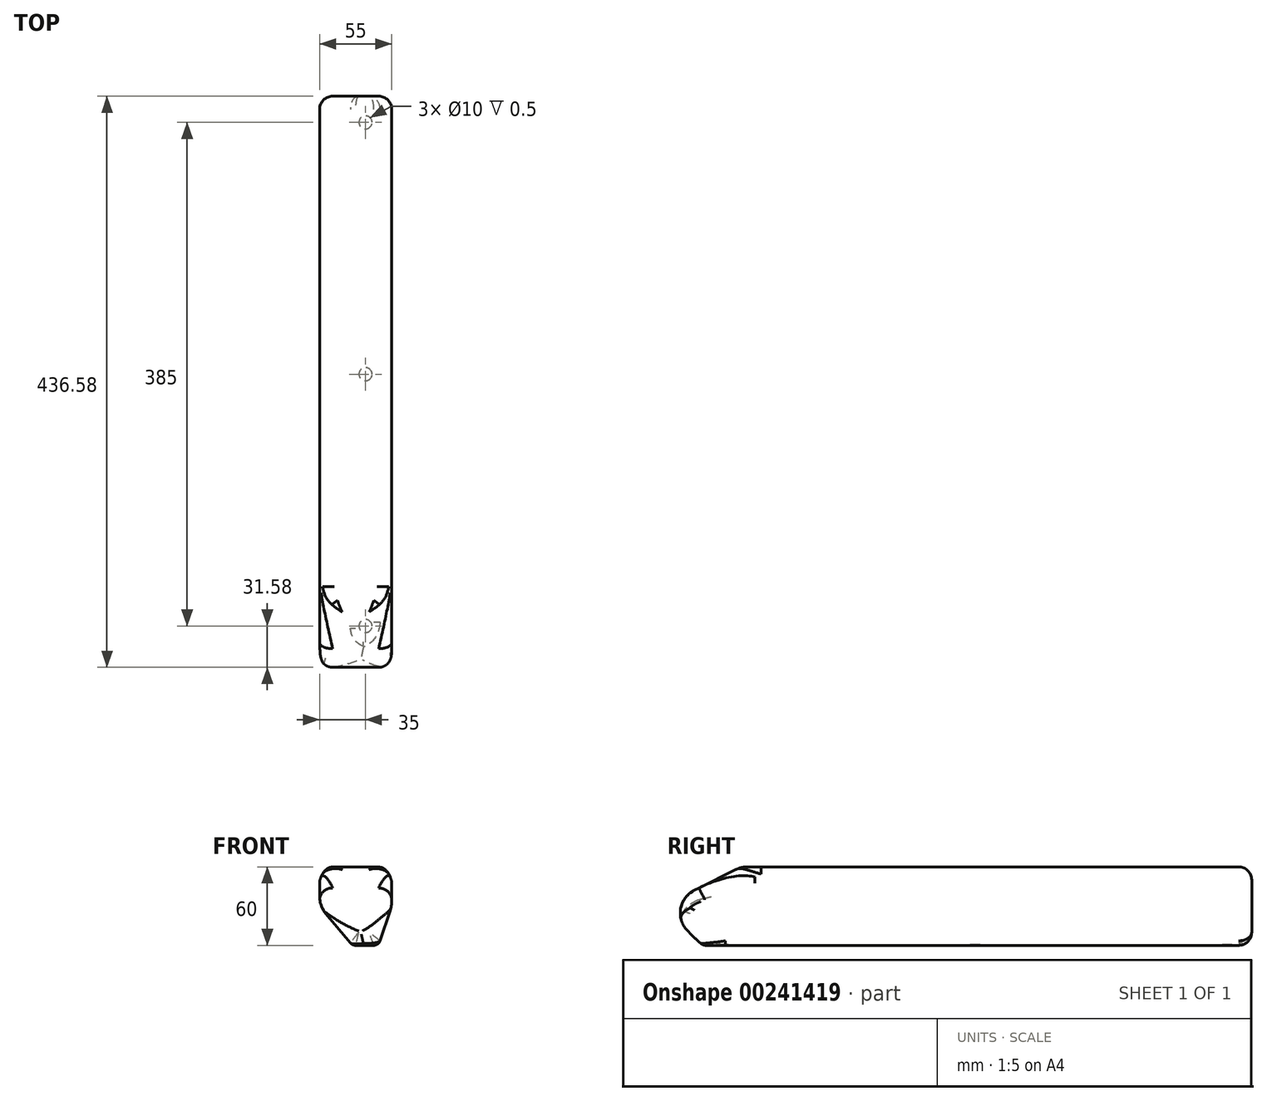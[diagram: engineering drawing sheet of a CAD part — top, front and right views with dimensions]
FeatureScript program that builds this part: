
annotation { "Feature Type Name" : "Feature", "Feature Type Description" : "" }
export const myFeature = defineFeature(function(context is Context, id is Id, definition is map)
    precondition{}
    {
        {
            var Q0;
            Q0=qCreatedBy(makeId("Top.planeOp"),FACE);
            var sketch = newSketch(context, id + "F0", { "sketchPlane" : qUnion([Q0])});
            skLineSegment(sketch, "E0.bottom", {"start": v(-27.5, 212.5) * mm, "end": v(27.5, 212.5) * mm});
            skLineSegment(sketch, "E0.top", {"start": v(-27.5, -237.5) * mm, "end": v(27.5, -237.5) * mm});
            skLineSegment(sketch, "E0.left", {"start": v(-27.5, 212.5) * mm, "end": v(-27.5, -237.5) * mm});
            skLineSegment(sketch, "E0.right", {"start": v(27.5, 212.5) * mm, "end": v(27.5, -237.5) * mm});
            skPoint(sketch, "E0.middle", {"position": v(0, 8.95) * mm});
            skSolve(sketch);
        }
        {
            var Q0;
            Q0=qSketchRegion(id+"F0",true);
            extrude(context, id + "F1", {"entities" : qUnion([Q0]), "depth" : 60 * mm});
        }
        {
            var Q0;
            Q0=makeQuery(id+"F1.opExtrude","CAP_FACE",FACE,{"disambiguationData":[OSD([sQuery(id+"F0.wireOp",EDGE,"E0.bottom"),sQuery(id+"F0.wireOp",EDGE,"E0.top"),sQuery(id+"F0.wireOp",EDGE,"E0.left"),sQuery(id+"F0.wireOp",EDGE,"E0.right")])],"isStart":true});
            var sketch = newSketch(context, id + "F2", { "sketchPlane" : qUnion([Q0])});
            skCircle(sketch, "E1", {"center": v(7.5, 192.5) * mm, "radius": 5 * mm});
            skCircle(sketch, "E2", {"center": v(7.5, -192.5) * mm, "radius": 5 * mm});
            skCircle(sketch, "E3", {"center": v(7.5, 0) * mm, "radius": 5 * mm});
            skSolve(sketch);
        }
        {
            var Q0;
            Q0=qSketchRegion(id+"F2",true);
            extrude(context, id + "F3", {"entities" : qUnion([Q0]), "operationType" : NewBodyOperationType.REMOVE, "oppositeDirection" : true, "depth" : .5 * mm});
        }
        {
            var Q0;
            Q0=makeQuery(id+"F1.opExtrude","CAP_EDGE",EDGE,{"disambiguationData":[OSD([sQuery(id+"F0.wireOp",EDGE,"E0.top")])],"isStart":false});
            chamfer(context, id + "F4", {"entities" : qUnion([Q0]), "chamferType" : ChamferType.TWO_OFFSETS, "width1" : 60 * mm, "oppositeDirection" : false, "width2" : 30 * mm});
        }
        {
            var Q0;
            Q0=makeQuery(id+"F1.opExtrude","CAP_EDGE",EDGE,{"disambiguationData":[OSD([sQuery(id+"F0.wireOp",EDGE,"E0.top")])],"isStart":true});
            chamfer(context, id + "F5", {"entities" : qUnion([Q0]), "chamferType" : ChamferType.TWO_OFFSETS, "width1" : 30 * mm, "oppositeDirection" : false, "width2" : 30 * mm, "tangentPropagation" : true});
        }
        {
            var Q0;
            Q0=makeQuery(id+"F1.opExtrude","CAP_EDGE",EDGE,{"disambiguationData":[OSD([sQuery(id+"F0.wireOp",EDGE,"E0.left")])],"isStart":true});
            chamfer(context, id + "F6", {"entities" : qUnion([Q0]), "chamferType" : ChamferType.TWO_OFFSETS, "width1" : 30 * mm, "oppositeDirection" : false, "width2" : 25 * mm, "tangentPropagation" : true});
        }
        {
            var Q0;
            Q0=makeQuery(id+"F1.opExtrude","CAP_EDGE",EDGE,{"disambiguationData":[OSD([sQuery(id+"F0.wireOp",EDGE,"E0.right")])],"isStart":true});
            chamfer(context, id + "F7", {"entities" : qUnion([Q0]), "chamferType" : ChamferType.TWO_OFFSETS, "width1" : 10 * mm, "oppositeDirection" : false, "width2" : 30 * mm, "tangentPropagation" : true});
        }
        {
            var Q0;
            Q0=makeQuery(id+"F1.opExtrude","CAP_EDGE",EDGE,{"disambiguationData":[OSD([sQuery(id+"F0.wireOp",EDGE,"E0.left")])],"isStart":false});
            var Q1;
            Q1=makeQuery(id+"F1.opExtrude","CAP_EDGE",EDGE,{"disambiguationData":[OSD([sQuery(id+"F0.wireOp",EDGE,"E0.right")])],"isStart":false});
            chamfer(context, id + "F8", {"entities" : qUnion([Q0, Q1]), "chamferType" : ChamferType.TWO_OFFSETS, "width1" : 5 * mm, "oppositeDirection" : false, "width2" : 10 * mm, "tangentPropagation" : true});
        }
        {
            var Q0;
            {var subQ0=sQuery(id+"F0.wireOp",EDGE,"E0.top");Q0=makeQuery(id+"F4.opChamfer","BLEND_EDGE",EDGE,{"blendedFrom":[makeQuery(id+"F1.opExtrude","CAP_EDGE",EDGE,{"disambiguationData":[OSD([subQ0])],"isStart":false}),makeQuery(id+"F1.opExtrude","CAP_FACE",FACE,{"disambiguationData":[OSD([sQuery(id+"F0.wireOp",EDGE,"E0.bottom"),subQ0,sQuery(id+"F0.wireOp",EDGE,"E0.left"),sQuery(id+"F0.wireOp",EDGE,"E0.right")])],"isStart":false})],"blendedInto":[makeQuery(id+"F1.opExtrude","CAP_FACE",FACE,{"disambiguationData":[OSD([sQuery(id+"F0.wireOp",EDGE,"E0.bottom"),subQ0,sQuery(id+"F0.wireOp",EDGE,"E0.left"),sQuery(id+"F0.wireOp",EDGE,"E0.right")])],"isStart":false})]});}
            var Q1;
            {var subQ0=sQuery(id+"F0.wireOp",EDGE,"E0.top");Q1=makeQuery(id+"F5.opChamfer","BLEND_EDGE",EDGE,{"blendedFrom":[makeQuery(id+"F1.opExtrude","CAP_EDGE",EDGE,{"disambiguationData":[OSD([subQ0])],"isStart":true}),makeQuery(id+"F4.opChamfer","BLEND_FACE",FACE,{"disambiguationData":[OSD([subQ0])]})],"blendedInto":[makeQuery(id+"F4.opChamfer","BLEND_FACE",FACE,{"disambiguationData":[OSD([subQ0])]})]});}
            var Q2;
            {var subQ0=sQuery(id+"F0.wireOp",EDGE,"E0.top");Q2=makeQuery(id+"F5.opChamfer","BLEND_EDGE",EDGE,{"blendedFrom":[makeQuery(id+"F1.opExtrude","CAP_EDGE",EDGE,{"disambiguationData":[OSD([subQ0])],"isStart":true}),makeQuery(id+"F1.opExtrude","CAP_FACE",FACE,{"disambiguationData":[OSD([sQuery(id+"F0.wireOp",EDGE,"E0.bottom"),subQ0,sQuery(id+"F0.wireOp",EDGE,"E0.left"),sQuery(id+"F0.wireOp",EDGE,"E0.right")])],"isStart":true})],"blendedInto":[makeQuery(id+"F1.opExtrude","CAP_FACE",FACE,{"disambiguationData":[OSD([sQuery(id+"F0.wireOp",EDGE,"E0.bottom"),subQ0,sQuery(id+"F0.wireOp",EDGE,"E0.left"),sQuery(id+"F0.wireOp",EDGE,"E0.right")])],"isStart":true})]});}
            var Q3;
            Q3=makeQuery(id+"F7.opChamfer","BLEND_EDGE",EDGE,{"blendedFrom":[makeQuery(id+"F1.opExtrude","CAP_EDGE",EDGE,{"disambiguationData":[OSD([sQuery(id+"F0.wireOp",EDGE,"E0.right")])],"isStart":true}),makeQuery(id+"F5.opChamfer","BLEND_FACE",FACE,{"disambiguationData":[OSD([sQuery(id+"F0.wireOp",EDGE,"E0.top")])]})],"blendedInto":[makeQuery(id+"F5.opChamfer","BLEND_FACE",FACE,{"disambiguationData":[OSD([sQuery(id+"F0.wireOp",EDGE,"E0.top")])]})]});
            var Q4;
            Q4=makeQuery(id+"F6.opChamfer","BLEND_EDGE",EDGE,{"blendedFrom":[makeQuery(id+"F1.opExtrude","CAP_EDGE",EDGE,{"disambiguationData":[OSD([sQuery(id+"F0.wireOp",EDGE,"E0.left")])],"isStart":true}),makeQuery(id+"F5.opChamfer","BLEND_FACE",FACE,{"disambiguationData":[OSD([sQuery(id+"F0.wireOp",EDGE,"E0.top")])]})],"blendedInto":[makeQuery(id+"F5.opChamfer","BLEND_FACE",FACE,{"disambiguationData":[OSD([sQuery(id+"F0.wireOp",EDGE,"E0.top")])]})]});
            var Q5;
            Q5=makeQuery(id+"F8.opChamfer","BLEND_EDGE",EDGE,{"blendedFrom":[makeQuery(id+"F1.opExtrude","CAP_EDGE",EDGE,{"disambiguationData":[OSD([sQuery(id+"F0.wireOp",EDGE,"E0.left")])],"isStart":false}),makeQuery(id+"F4.opChamfer","BLEND_FACE",FACE,{"disambiguationData":[OSD([sQuery(id+"F0.wireOp",EDGE,"E0.top")])]})],"blendedInto":[makeQuery(id+"F4.opChamfer","BLEND_FACE",FACE,{"disambiguationData":[OSD([sQuery(id+"F0.wireOp",EDGE,"E0.top")])]})]});
            var Q6;
            Q6=makeQuery(id+"F8.opChamfer","BLEND_EDGE",EDGE,{"blendedFrom":[makeQuery(id+"F1.opExtrude","CAP_EDGE",EDGE,{"disambiguationData":[OSD([sQuery(id+"F0.wireOp",EDGE,"E0.right")])],"isStart":false}),makeQuery(id+"F4.opChamfer","BLEND_FACE",FACE,{"disambiguationData":[OSD([sQuery(id+"F0.wireOp",EDGE,"E0.top")])]})],"blendedInto":[makeQuery(id+"F4.opChamfer","BLEND_FACE",FACE,{"disambiguationData":[OSD([sQuery(id+"F0.wireOp",EDGE,"E0.top")])]})]});
            fillet(context, id + "F9", {"entities" : qUnion([Q0, Q1, Q2, Q3, Q4, Q5, Q6]), "radius" : 19.5 * mm, "tangentPropagation" : true, "allowEdgeOverflow" : false});
        }
        {
            var Q0;
            {var subQ0=sQuery(id+"F0.wireOp",EDGE,"E0.left");Q0=makeQuery(id+"F6.opChamfer","BLEND_EDGE",EDGE,{"blendedFrom":[makeQuery(id+"F1.opExtrude","CAP_EDGE",EDGE,{"disambiguationData":[OSD([subQ0])],"isStart":true}),makeQuery(id+"F1.opExtrude","CAP_FACE",FACE,{"disambiguationData":[OSD([sQuery(id+"F0.wireOp",EDGE,"E0.bottom"),sQuery(id+"F0.wireOp",EDGE,"E0.top"),subQ0,sQuery(id+"F0.wireOp",EDGE,"E0.right")])],"isStart":true})],"blendedInto":[makeQuery(id+"F1.opExtrude","CAP_FACE",FACE,{"disambiguationData":[OSD([sQuery(id+"F0.wireOp",EDGE,"E0.bottom"),sQuery(id+"F0.wireOp",EDGE,"E0.top"),subQ0,sQuery(id+"F0.wireOp",EDGE,"E0.right")])],"isStart":true})]});}
            var Q1;
            {var subQ0=sQuery(id+"F0.wireOp",EDGE,"E0.right");Q1=makeQuery(id+"F7.opChamfer","BLEND_EDGE",EDGE,{"blendedFrom":[makeQuery(id+"F1.opExtrude","CAP_EDGE",EDGE,{"disambiguationData":[OSD([subQ0])],"isStart":true}),makeQuery(id+"F1.opExtrude","CAP_FACE",FACE,{"disambiguationData":[OSD([sQuery(id+"F0.wireOp",EDGE,"E0.bottom"),sQuery(id+"F0.wireOp",EDGE,"E0.top"),sQuery(id+"F0.wireOp",EDGE,"E0.left"),subQ0])],"isStart":true})],"blendedInto":[makeQuery(id+"F1.opExtrude","CAP_FACE",FACE,{"disambiguationData":[OSD([sQuery(id+"F0.wireOp",EDGE,"E0.bottom"),sQuery(id+"F0.wireOp",EDGE,"E0.top"),sQuery(id+"F0.wireOp",EDGE,"E0.left"),subQ0])],"isStart":true})]});}
            fillet(context, id + "F10", {"entities" : qUnion([Q0, Q1]), "radius" : 5 * mm, "tangentPropagation" : true, "allowEdgeOverflow" : false});
        }
        {
            var Q0;
            {var subQ0=sQuery(id+"F0.wireOp",EDGE,"E0.left");Q0=makeQuery(id+"F9.opFillet","BLEND_EDGE",EDGE,{"blendedFrom":[makeQuery(id+"F6.opChamfer","BLEND_EDGE",EDGE,{"blendedFrom":[makeQuery(id+"F1.opExtrude","CAP_EDGE",EDGE,{"disambiguationData":[OSD([subQ0])],"isStart":true}),makeQuery(id+"F5.opChamfer","BLEND_FACE",FACE,{"disambiguationData":[OSD([sQuery(id+"F0.wireOp",EDGE,"E0.top")])]})],"blendedInto":[makeQuery(id+"F5.opChamfer","BLEND_FACE",FACE,{"disambiguationData":[OSD([sQuery(id+"F0.wireOp",EDGE,"E0.top")])]})]}),makeQuery(id+"F6.opChamfer","BLEND_FACE",FACE,{"disambiguationData":[OSD([subQ0])]})],"blendedInto":[makeQuery(id+"F6.opChamfer","BLEND_FACE",FACE,{"disambiguationData":[OSD([subQ0])]})]});}
            var Q1;
            {var subQ0=sQuery(id+"F0.wireOp",EDGE,"E0.top");Q1=makeQuery(id+"F9.opFillet","BLEND_EDGE",EDGE,{"blendedFrom":[makeQuery(id+"F5.opChamfer","BLEND_EDGE",EDGE,{"blendedFrom":[makeQuery(id+"F1.opExtrude","CAP_EDGE",EDGE,{"disambiguationData":[OSD([subQ0])],"isStart":true}),makeQuery(id+"F4.opChamfer","BLEND_FACE",FACE,{"disambiguationData":[OSD([subQ0])]})],"blendedInto":[makeQuery(id+"F4.opChamfer","BLEND_FACE",FACE,{"disambiguationData":[OSD([subQ0])]})]}),makeQuery(id+"F1.opExtrude","SWEPT_FACE",FACE,{"disambiguationData":[OSD([sQuery(id+"F0.wireOp",EDGE,"E0.left")])]})],"blendedInto":[makeQuery(id+"F1.opExtrude","SWEPT_FACE",FACE,{"disambiguationData":[OSD([sQuery(id+"F0.wireOp",EDGE,"E0.left")])]})]});}
            var Q2;
            {var subQ0=sQuery(id+"F0.wireOp",EDGE,"E0.left");Q2=makeQuery(id+"F9.opFillet","BLEND_EDGE",EDGE,{"blendedFrom":[makeQuery(id+"F8.opChamfer","BLEND_EDGE",EDGE,{"blendedFrom":[makeQuery(id+"F1.opExtrude","CAP_EDGE",EDGE,{"disambiguationData":[OSD([subQ0])],"isStart":false}),makeQuery(id+"F4.opChamfer","BLEND_FACE",FACE,{"disambiguationData":[OSD([sQuery(id+"F0.wireOp",EDGE,"E0.top")])]})],"blendedInto":[makeQuery(id+"F4.opChamfer","BLEND_FACE",FACE,{"disambiguationData":[OSD([sQuery(id+"F0.wireOp",EDGE,"E0.top")])]})]}),makeQuery(id+"F1.opExtrude","SWEPT_FACE",FACE,{"disambiguationData":[OSD([subQ0])]})],"blendedInto":[makeQuery(id+"F1.opExtrude","SWEPT_FACE",FACE,{"disambiguationData":[OSD([subQ0])]})]});}
            var Q3;
            {var subQ0=sQuery(id+"F0.wireOp",EDGE,"E0.left");Q3=makeQuery(id+"F9.opFillet","BLEND_EDGE",EDGE,{"blendedFrom":[makeQuery(id+"F8.opChamfer","BLEND_EDGE",EDGE,{"blendedFrom":[makeQuery(id+"F1.opExtrude","CAP_EDGE",EDGE,{"disambiguationData":[OSD([subQ0])],"isStart":false}),makeQuery(id+"F4.opChamfer","BLEND_FACE",FACE,{"disambiguationData":[OSD([sQuery(id+"F0.wireOp",EDGE,"E0.top")])]})],"blendedInto":[makeQuery(id+"F4.opChamfer","BLEND_FACE",FACE,{"disambiguationData":[OSD([sQuery(id+"F0.wireOp",EDGE,"E0.top")])]})]}),makeQuery(id+"F8.opChamfer","BLEND_FACE",FACE,{"disambiguationData":[OSD([subQ0])]})],"blendedInto":[makeQuery(id+"F8.opChamfer","BLEND_FACE",FACE,{"disambiguationData":[OSD([subQ0])]})]});}
            var Q4;
            {var subQ0=sQuery(id+"F0.wireOp",EDGE,"E0.right");Q4=makeQuery(id+"F9.opFillet","BLEND_EDGE",EDGE,{"blendedFrom":[makeQuery(id+"F8.opChamfer","BLEND_EDGE",EDGE,{"blendedFrom":[makeQuery(id+"F1.opExtrude","CAP_EDGE",EDGE,{"disambiguationData":[OSD([subQ0])],"isStart":false}),makeQuery(id+"F4.opChamfer","BLEND_FACE",FACE,{"disambiguationData":[OSD([sQuery(id+"F0.wireOp",EDGE,"E0.top")])]})],"blendedInto":[makeQuery(id+"F4.opChamfer","BLEND_FACE",FACE,{"disambiguationData":[OSD([sQuery(id+"F0.wireOp",EDGE,"E0.top")])]})]}),makeQuery(id+"F8.opChamfer","BLEND_FACE",FACE,{"disambiguationData":[OSD([subQ0])]})],"blendedInto":[makeQuery(id+"F8.opChamfer","BLEND_FACE",FACE,{"disambiguationData":[OSD([subQ0])]})]});}
            var Q5;
            {var subQ0=sQuery(id+"F0.wireOp",EDGE,"E0.right");Q5=makeQuery(id+"F9.opFillet","BLEND_EDGE",EDGE,{"blendedFrom":[makeQuery(id+"F8.opChamfer","BLEND_EDGE",EDGE,{"blendedFrom":[makeQuery(id+"F1.opExtrude","CAP_EDGE",EDGE,{"disambiguationData":[OSD([subQ0])],"isStart":false}),makeQuery(id+"F4.opChamfer","BLEND_FACE",FACE,{"disambiguationData":[OSD([sQuery(id+"F0.wireOp",EDGE,"E0.top")])]})],"blendedInto":[makeQuery(id+"F4.opChamfer","BLEND_FACE",FACE,{"disambiguationData":[OSD([sQuery(id+"F0.wireOp",EDGE,"E0.top")])]})]}),makeQuery(id+"F1.opExtrude","SWEPT_FACE",FACE,{"disambiguationData":[OSD([subQ0])]})],"blendedInto":[makeQuery(id+"F1.opExtrude","SWEPT_FACE",FACE,{"disambiguationData":[OSD([subQ0])]})]});}
            var Q6;
            {var subQ0=sQuery(id+"F0.wireOp",EDGE,"E0.top");Q6=makeQuery(id+"F9.opFillet","BLEND_EDGE",EDGE,{"blendedFrom":[makeQuery(id+"F5.opChamfer","BLEND_EDGE",EDGE,{"blendedFrom":[makeQuery(id+"F1.opExtrude","CAP_EDGE",EDGE,{"disambiguationData":[OSD([subQ0])],"isStart":true}),makeQuery(id+"F4.opChamfer","BLEND_FACE",FACE,{"disambiguationData":[OSD([subQ0])]})],"blendedInto":[makeQuery(id+"F4.opChamfer","BLEND_FACE",FACE,{"disambiguationData":[OSD([subQ0])]})]}),makeQuery(id+"F1.opExtrude","SWEPT_FACE",FACE,{"disambiguationData":[OSD([sQuery(id+"F0.wireOp",EDGE,"E0.right")])]})],"blendedInto":[makeQuery(id+"F1.opExtrude","SWEPT_FACE",FACE,{"disambiguationData":[OSD([sQuery(id+"F0.wireOp",EDGE,"E0.right")])]})]});}
            var Q7;
            {var subQ0=sQuery(id+"F0.wireOp",EDGE,"E0.right");Q7=makeQuery(id+"F9.opFillet","BLEND_EDGE",EDGE,{"blendedFrom":[makeQuery(id+"F7.opChamfer","BLEND_EDGE",EDGE,{"blendedFrom":[makeQuery(id+"F1.opExtrude","CAP_EDGE",EDGE,{"disambiguationData":[OSD([subQ0])],"isStart":true}),makeQuery(id+"F5.opChamfer","BLEND_FACE",FACE,{"disambiguationData":[OSD([sQuery(id+"F0.wireOp",EDGE,"E0.top")])]})],"blendedInto":[makeQuery(id+"F5.opChamfer","BLEND_FACE",FACE,{"disambiguationData":[OSD([sQuery(id+"F0.wireOp",EDGE,"E0.top")])]})]}),makeQuery(id+"F7.opChamfer","BLEND_FACE",FACE,{"disambiguationData":[OSD([subQ0])]})],"blendedInto":[makeQuery(id+"F7.opChamfer","BLEND_FACE",FACE,{"disambiguationData":[OSD([subQ0])]})]});}
            fillet(context, id + "F11", {"entities" : qUnion([Q0, Q1, Q2, Q3, Q4, Q5, Q6, Q7]), "radius" : 10 * mm, "tangentPropagation" : true, "allowEdgeOverflow" : false});
        }
        {
            var Q0;
            {var subQ0=sQuery(id+"F0.wireOp",EDGE,"E0.right");Q0=makeQuery(id+"F7.opChamfer","BLEND_EDGE",EDGE,{"blendedFrom":[makeQuery(id+"F1.opExtrude","CAP_EDGE",EDGE,{"disambiguationData":[OSD([subQ0])],"isStart":true}),makeQuery(id+"F1.opExtrude","SWEPT_FACE",FACE,{"disambiguationData":[OSD([subQ0])]})],"blendedInto":[makeQuery(id+"F1.opExtrude","SWEPT_FACE",FACE,{"disambiguationData":[OSD([subQ0])]})]});}
            var Q1;
            {var subQ0=sQuery(id+"F0.wireOp",EDGE,"E0.right");var subQ1=makeQuery(id+"F1.opExtrude","SWEPT_FACE",FACE,{"disambiguationData":[OSD([subQ0])]});Q1=makeQuery(id+"F11.opFillet","BLEND_EDGE",EDGE,{"blendedFrom":[makeQuery(id+"F8.opChamfer","BLEND_EDGE",EDGE,{"blendedFrom":[makeQuery(id+"F1.opExtrude","CAP_EDGE",EDGE,{"disambiguationData":[OSD([subQ0])],"isStart":false}),subQ1],"blendedInto":[subQ1]}),subQ1],"blendedInto":[subQ1]});}
            var Q2;
            {var subQ0=sQuery(id+"F0.wireOp",EDGE,"E0.right");Q2=makeQuery(id+"F11.opFillet","BLEND_EDGE",EDGE,{"blendedFrom":[makeQuery(id+"F8.opChamfer","BLEND_EDGE",EDGE,{"blendedFrom":[makeQuery(id+"F1.opExtrude","CAP_EDGE",EDGE,{"disambiguationData":[OSD([subQ0])],"isStart":false}),makeQuery(id+"F1.opExtrude","SWEPT_FACE",FACE,{"disambiguationData":[OSD([subQ0])]})],"blendedInto":[makeQuery(id+"F1.opExtrude","SWEPT_FACE",FACE,{"disambiguationData":[OSD([subQ0])]})]}),makeQuery(id+"F8.opChamfer","BLEND_FACE",FACE,{"disambiguationData":[OSD([subQ0])]})],"blendedInto":[makeQuery(id+"F8.opChamfer","BLEND_FACE",FACE,{"disambiguationData":[OSD([subQ0])]})]});}
            var Q3;
            {var subQ0=sQuery(id+"F0.wireOp",EDGE,"E0.right");Q3=makeQuery(id+"F10.opFillet","BLEND_EDGE",EDGE,{"blendedFrom":[makeQuery(id+"F7.opChamfer","BLEND_EDGE",EDGE,{"blendedFrom":[makeQuery(id+"F1.opExtrude","CAP_EDGE",EDGE,{"disambiguationData":[OSD([subQ0])],"isStart":true}),makeQuery(id+"F1.opExtrude","CAP_FACE",FACE,{"disambiguationData":[OSD([sQuery(id+"F0.wireOp",EDGE,"E0.bottom"),sQuery(id+"F0.wireOp",EDGE,"E0.top"),sQuery(id+"F0.wireOp",EDGE,"E0.left"),subQ0])],"isStart":true})],"blendedInto":[makeQuery(id+"F1.opExtrude","CAP_FACE",FACE,{"disambiguationData":[OSD([sQuery(id+"F0.wireOp",EDGE,"E0.bottom"),sQuery(id+"F0.wireOp",EDGE,"E0.top"),sQuery(id+"F0.wireOp",EDGE,"E0.left"),subQ0])],"isStart":true})]}),makeQuery(id+"F7.opChamfer","BLEND_FACE",FACE,{"disambiguationData":[OSD([subQ0])]})],"blendedInto":[makeQuery(id+"F7.opChamfer","BLEND_FACE",FACE,{"disambiguationData":[OSD([subQ0])]})]});}
            var Q4;
            {var subQ0=sQuery(id+"F0.wireOp",EDGE,"E0.left");Q4=makeQuery(id+"F10.opFillet","BLEND_EDGE",EDGE,{"blendedFrom":[makeQuery(id+"F6.opChamfer","BLEND_EDGE",EDGE,{"blendedFrom":[makeQuery(id+"F1.opExtrude","CAP_EDGE",EDGE,{"disambiguationData":[OSD([subQ0])],"isStart":true}),makeQuery(id+"F1.opExtrude","CAP_FACE",FACE,{"disambiguationData":[OSD([sQuery(id+"F0.wireOp",EDGE,"E0.bottom"),sQuery(id+"F0.wireOp",EDGE,"E0.top"),subQ0,sQuery(id+"F0.wireOp",EDGE,"E0.right")])],"isStart":true})],"blendedInto":[makeQuery(id+"F1.opExtrude","CAP_FACE",FACE,{"disambiguationData":[OSD([sQuery(id+"F0.wireOp",EDGE,"E0.bottom"),sQuery(id+"F0.wireOp",EDGE,"E0.top"),subQ0,sQuery(id+"F0.wireOp",EDGE,"E0.right")])],"isStart":true})]}),makeQuery(id+"F6.opChamfer","BLEND_FACE",FACE,{"disambiguationData":[OSD([subQ0])]})],"blendedInto":[makeQuery(id+"F6.opChamfer","BLEND_FACE",FACE,{"disambiguationData":[OSD([subQ0])]})]});}
            var Q5;
            {var subQ0=sQuery(id+"F0.wireOp",EDGE,"E0.left");Q5=makeQuery(id+"F6.opChamfer","BLEND_EDGE",EDGE,{"blendedFrom":[makeQuery(id+"F1.opExtrude","CAP_EDGE",EDGE,{"disambiguationData":[OSD([subQ0])],"isStart":true}),makeQuery(id+"F1.opExtrude","SWEPT_FACE",FACE,{"disambiguationData":[OSD([subQ0])]})],"blendedInto":[makeQuery(id+"F1.opExtrude","SWEPT_FACE",FACE,{"disambiguationData":[OSD([subQ0])]})]});}
            var Q6;
            {var subQ0=sQuery(id+"F0.wireOp",EDGE,"E0.left");var subQ1=makeQuery(id+"F1.opExtrude","SWEPT_FACE",FACE,{"disambiguationData":[OSD([subQ0])]});Q6=makeQuery(id+"F11.opFillet","BLEND_EDGE",EDGE,{"blendedFrom":[makeQuery(id+"F8.opChamfer","BLEND_EDGE",EDGE,{"blendedFrom":[makeQuery(id+"F1.opExtrude","CAP_EDGE",EDGE,{"disambiguationData":[OSD([subQ0])],"isStart":false}),subQ1],"blendedInto":[subQ1]}),subQ1],"blendedInto":[subQ1]});}
            fillet(context, id + "F12", {"entities" : qUnion([Q0, Q1, Q2, Q3, Q4, Q5, Q6]), "radius" : 20 * mm, "allowEdgeOverflow" : false});
        }
        {
            var Q0;
            {var subQ0=sQuery(id+"F0.wireOp",EDGE,"E0.right");Q0=makeQuery(id+"F8.opChamfer","BLEND_EDGE",EDGE,{"blendedFrom":[makeQuery(id+"F1.opExtrude","CAP_EDGE",EDGE,{"disambiguationData":[OSD([subQ0])],"isStart":false}),makeQuery(id+"F1.opExtrude","CAP_FACE",FACE,{"disambiguationData":[OSD([sQuery(id+"F0.wireOp",EDGE,"E0.bottom"),sQuery(id+"F0.wireOp",EDGE,"E0.top"),sQuery(id+"F0.wireOp",EDGE,"E0.left"),subQ0])],"isStart":false})],"blendedInto":[makeQuery(id+"F1.opExtrude","CAP_FACE",FACE,{"disambiguationData":[OSD([sQuery(id+"F0.wireOp",EDGE,"E0.bottom"),sQuery(id+"F0.wireOp",EDGE,"E0.top"),sQuery(id+"F0.wireOp",EDGE,"E0.left"),subQ0])],"isStart":false})]});}
            var Q1;
            {var subQ0=sQuery(id+"F0.wireOp",EDGE,"E0.left");Q1=makeQuery(id+"F8.opChamfer","BLEND_EDGE",EDGE,{"blendedFrom":[makeQuery(id+"F1.opExtrude","CAP_EDGE",EDGE,{"disambiguationData":[OSD([subQ0])],"isStart":false}),makeQuery(id+"F1.opExtrude","CAP_FACE",FACE,{"disambiguationData":[OSD([sQuery(id+"F0.wireOp",EDGE,"E0.bottom"),sQuery(id+"F0.wireOp",EDGE,"E0.top"),subQ0,sQuery(id+"F0.wireOp",EDGE,"E0.right")])],"isStart":false})],"blendedInto":[makeQuery(id+"F1.opExtrude","CAP_FACE",FACE,{"disambiguationData":[OSD([sQuery(id+"F0.wireOp",EDGE,"E0.bottom"),sQuery(id+"F0.wireOp",EDGE,"E0.top"),subQ0,sQuery(id+"F0.wireOp",EDGE,"E0.right")])],"isStart":false})]});}
            fillet(context, id + "F13", {"entities" : qUnion([Q0, Q1]), "radius" : 10 * mm, "tangentPropagation" : true, "allowEdgeOverflow" : false});
        }
        {
            var Q0;
            Q0=makeQuery(id+"F1.opExtrude","SWEPT_FACE",FACE,{"disambiguationData":[OSD([sQuery(id+"F0.wireOp",EDGE,"E0.bottom")])]});
            fillet(context, id + "F14", {"entities" : qUnion([Q0]), "radius" : 10 * mm, "tangentPropagation" : true, "allowEdgeOverflow" : false});
        }
    });
